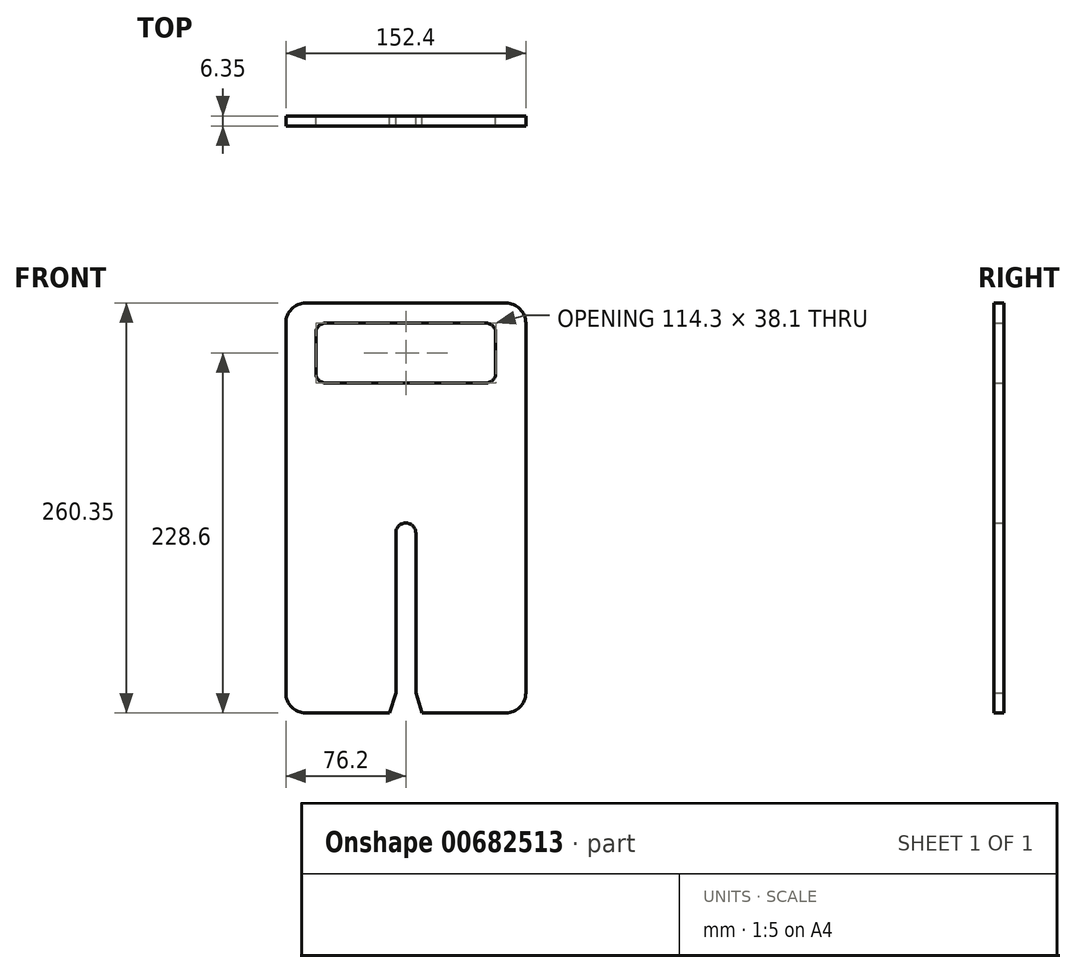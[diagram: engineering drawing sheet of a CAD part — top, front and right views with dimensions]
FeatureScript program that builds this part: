
annotation { "Feature Type Name" : "Feature", "Feature Type Description" : "" }
export const myFeature = defineFeature(function(context is Context, id is Id, definition is map)
    precondition{}
    {
        {
            var Q0;
            Q0=qCreatedBy(makeId("Front.planeOp"),FACE);
            var sketch = newSketch(context, id + "F0", { "sketchPlane" : qUnion([Q0])});
            skArc(sketch, "E0", {"start": v(6.35, 0) * mm, "mid": v(0, 6.35) * mm, "end": v(-6.35, 0) * mm});
            skLineSegment(sketch, "E1", {"start": v(-6.35, 0) * mm, "end": v(-6.35, -101.6) * mm});
            skLineSegment(sketch, "E2", {"start": v(6.35, 0) * mm, "end": v(6.35, -101.6) * mm});
            skLineSegment(sketch, "E3", {"start": v(-6.35, -101.6) * mm, "end": v(-10.32, -114.3) * mm});
            skLineSegment(sketch, "E4", {"start": v(6.35, -101.6) * mm, "end": v(10.32, -114.3) * mm});
            skLineSegment(sketch, "E5", {"start": v(10.32, -114.3) * mm, "end": v(63.5, -114.3) * mm});
            skLineSegment(sketch, "E6", {"start": v(76.2, -101.6) * mm, "end": v(76.2, 133.35) * mm});
            skLineSegment(sketch, "E7", {"start": v(63.5, 146.05) * mm, "end": v(-63.5, 146.05) * mm});
            skLineSegment(sketch, "E8", {"start": v(-76.2, 133.35) * mm, "end": v(-76.2, -101.6) * mm});
            skLineSegment(sketch, "E9", {"start": v(-63.5, -114.3) * mm, "end": v(-10.32, -114.3) * mm});
            skLineSegment(sketch, "E10.bottom", {"start": v(-50.8, 133.35) * mm, "end": v(50.8, 133.35) * mm});
            skLineSegment(sketch, "E10.top", {"start": v(-50.8, 95.25) * mm, "end": v(50.8, 95.25) * mm});
            skLineSegment(sketch, "E10.left", {"start": v(-57.15, 127) * mm, "end": v(-57.15, 101.6) * mm});
            skLineSegment(sketch, "E10.right", {"start": v(57.15, 127) * mm, "end": v(57.15, 101.6) * mm});
            skPoint(sketch, "E11.visualSharp", {"position": v(-57.15, 133.35) * mm});
            skArc(sketch, "E11.filletArc", {"start": v(-50.8, 133.35) * mm, "mid": v(-55.3, 131.5) * mm, "end": v(-57.15, 127) * mm});
            skPoint(sketch, "E12.visualSharp", {"position": v(57.15, 133.35) * mm});
            skArc(sketch, "E12.filletArc", {"start": v(57.15, 127) * mm, "mid": v(55.3, 131.5) * mm, "end": v(50.8, 133.35) * mm});
            skPoint(sketch, "E13.visualSharp", {"position": v(-57.15, 95.25) * mm});
            skArc(sketch, "E13.filletArc", {"start": v(-57.15, 101.6) * mm, "mid": v(-55.3, 97.1) * mm, "end": v(-50.8, 95.25) * mm});
            skPoint(sketch, "E14.visualSharp", {"position": v(57.15, 95.25) * mm});
            skArc(sketch, "E14.filletArc", {"start": v(50.8, 95.25) * mm, "mid": v(55.3, 97.1) * mm, "end": v(57.15, 101.6) * mm});
            skPoint(sketch, "E15.visualSharp", {"position": v(-76.2, 146.05) * mm});
            skArc(sketch, "E15.filletArc", {"start": v(-63.5, 146.05) * mm, "mid": v(-72.48, 142.33) * mm, "end": v(-76.2, 133.35) * mm});
            skPoint(sketch, "E16.visualSharp", {"position": v(76.2, 146.05) * mm});
            skArc(sketch, "E16.filletArc", {"start": v(76.2, 133.35) * mm, "mid": v(72.48, 142.33) * mm, "end": v(63.5, 146.05) * mm});
            skPoint(sketch, "E17.visualSharp", {"position": v(76.2, -114.3) * mm});
            skArc(sketch, "E17.filletArc", {"start": v(63.5, -114.3) * mm, "mid": v(72.48, -110.58) * mm, "end": v(76.2, -101.6) * mm});
            skPoint(sketch, "E18.visualSharp", {"position": v(-76.2, -114.3) * mm});
            skArc(sketch, "E18.filletArc", {"start": v(-76.2, -101.6) * mm, "mid": v(-72.48, -110.58) * mm, "end": v(-63.5, -114.3) * mm});
            skSolve(sketch);
        }
        {
            var Q0;
            Q0=makeQuery(id+"F0.imprint","IMPRINT",FACE,{"disambiguationData":[TD([[makeQuery(id+"F0.imprint","IMPRINT",EDGE,{"derivedFrom":sQuery(id+"F0.wireOp",EDGE,"E0")}),-1.0]])]});
            extrude(context, id + "F1", {"entities" : qUnion([Q0]), "depth" : 6.35 * mm, "offsetDistance" : 25.4 * mm});
        }
    });
